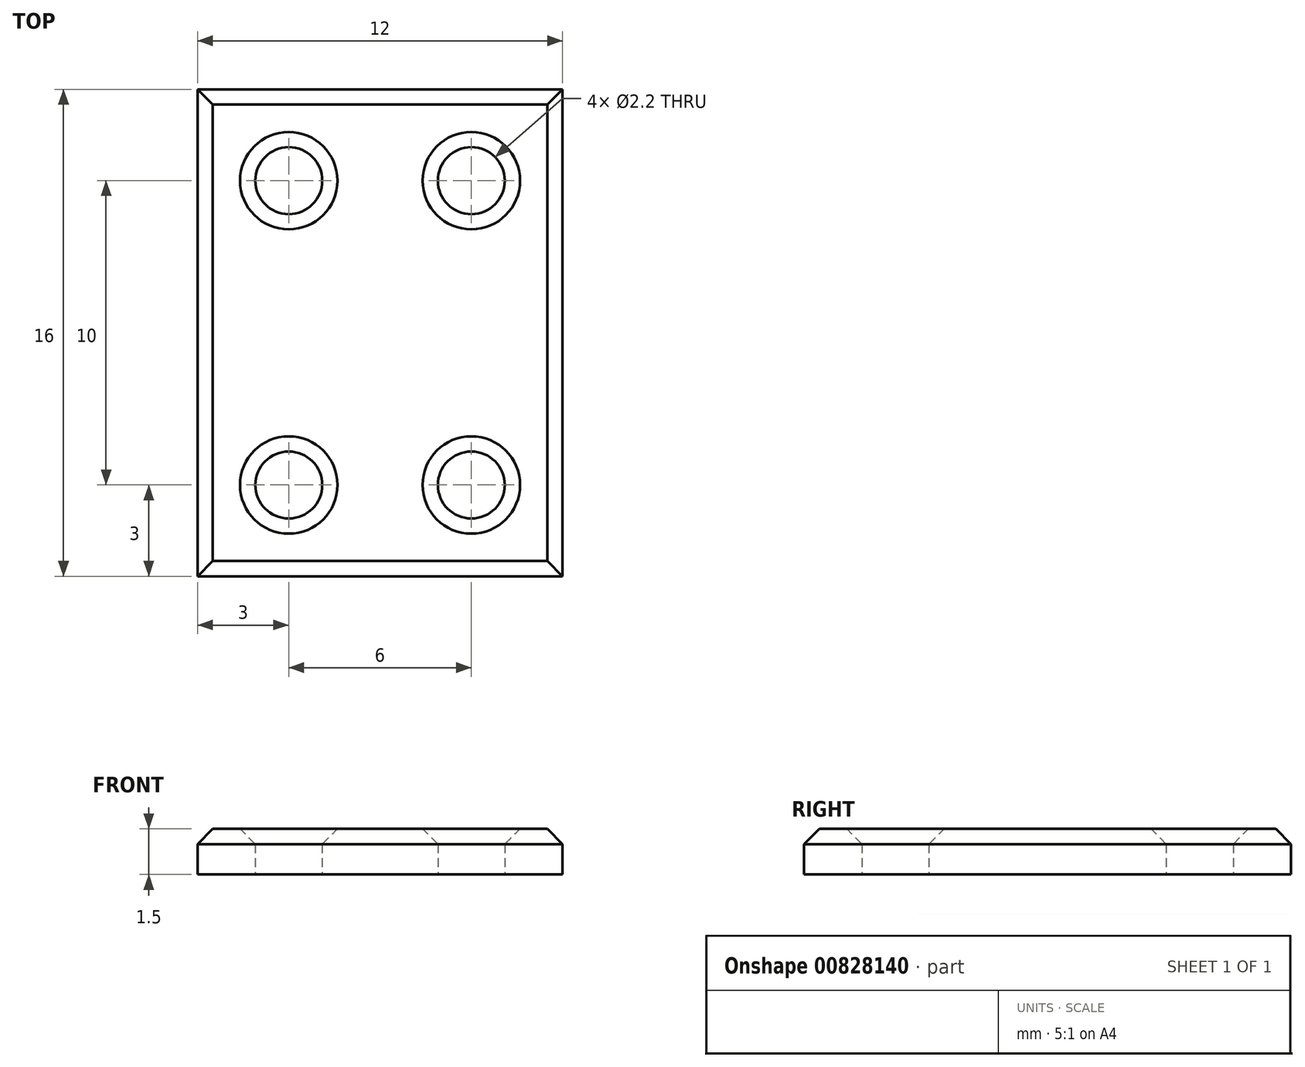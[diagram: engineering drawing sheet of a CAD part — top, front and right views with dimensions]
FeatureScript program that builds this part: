
annotation { "Feature Type Name" : "Feature", "Feature Type Description" : "" }
export const myFeature = defineFeature(function(context is Context, id is Id, definition is map)
    precondition{}
    {
        {
            var Q0;
            Q0=qCreatedBy(makeId("Top.planeOp"),FACE);
            var sketch = newSketch(context, id + "F0", { "sketchPlane" : qUnion([Q0])});
            skLineSegment(sketch, "E0.bottom", {"start": v(0, 0) * mm, "end": v(12, 0) * mm});
            skLineSegment(sketch, "E0.top", {"start": v(0, 16) * mm, "end": v(12, 16) * mm});
            skLineSegment(sketch, "E0.left", {"start": v(0, 0) * mm, "end": v(0, 16) * mm});
            skLineSegment(sketch, "E0.right", {"start": v(12, 0) * mm, "end": v(12, 16) * mm});
            skCircle(sketch, "E1", {"center": v(3, 13) * mm, "radius": 1.1 * mm});
            skCircle(sketch, "E2", {"center": v(9, 13) * mm, "radius": 1.1 * mm});
            skCircle(sketch, "E3", {"center": v(9, 3) * mm, "radius": 1.1 * mm});
            skCircle(sketch, "E4", {"center": v(3, 3) * mm, "radius": 1.1 * mm});
            skSolve(sketch);
        }
        {
            var Q0;
            Q0 = qSketchRegion(id + "F0", true);
            extrude(context, id + "F1", {"entities" : qUnion([Q0]), "depth" : 1.5 * mm, "offsetDistance" : 25 * mm});
        }
        {
            var Q0;
            Q0=makeQuery(id+"F1.opExtrude","CAP_FACE",FACE,{"disambiguationData":[OSD([sQuery(id+"F0.wireOp",EDGE,"E0.bottom"),sQuery(id+"F0.wireOp",EDGE,"E0.top"),sQuery(id+"F0.wireOp",EDGE,"E0.left"),sQuery(id+"F0.wireOp",EDGE,"E0.right"),sQuery(id+"F0.wireOp",EDGE,"E1"),sQuery(id+"F0.wireOp",EDGE,"E2"),sQuery(id+"F0.wireOp",EDGE,"E3"),sQuery(id+"F0.wireOp",EDGE,"E4")])],"isStart":false});
            var Q1;
            Q1=makeQuery(id+"F1.opExtrude","CAP_EDGE",EDGE,{"disambiguationData":[OSD([sQuery(id+"F0.wireOp",EDGE,"E0.top")])],"isStart":false});
            var Q2;
            Q2=makeQuery(id+"F1.opExtrude","CAP_EDGE",EDGE,{"disambiguationData":[OSD([sQuery(id+"F0.wireOp",EDGE,"E0.left")])],"isStart":false});
            var Q3;
            Q3=makeQuery(id+"F1.opExtrude","CAP_EDGE",EDGE,{"disambiguationData":[OSD([sQuery(id+"F0.wireOp",EDGE,"E0.bottom")])],"isStart":false});
            chamfer(context, id + "F2", {"entities" : qUnion([Q0, Q1, Q2, Q3]), "width" : 0.5 * mm, "tangentPropagation" : true});
        }
    });
